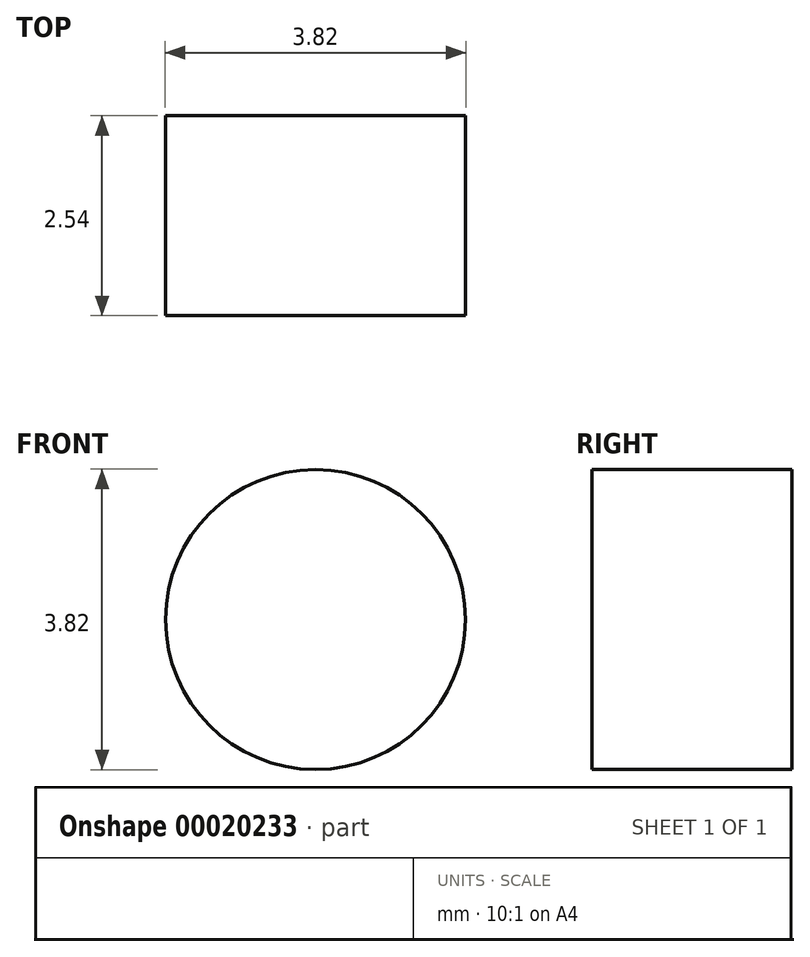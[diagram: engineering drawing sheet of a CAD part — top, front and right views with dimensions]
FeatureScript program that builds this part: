
annotation { "Feature Type Name" : "Feature", "Feature Type Description" : "" }
export const myFeature = defineFeature(function(context is Context, id is Id, definition is map)
    precondition{}
    {
        {
            var Q0;
            Q0=qCreatedBy(makeId("Front.planeOp"),FACE);
            var sketch = newSketch(context, id + "F0", { "sketchPlane" : qUnion([Q0])});
            skCircle(sketch, "E0", {"center": v(0, 0) * mm, "radius": 1.9 * mm});
            skSolve(sketch);
        }
        {
            var Q0;
            Q0 = qSketchRegion(id + "F0", true);
            extrude(context, id + "F1", {"entities" : qUnion([Q0]), "depth" : 2.54 * mm});
        }
    });
